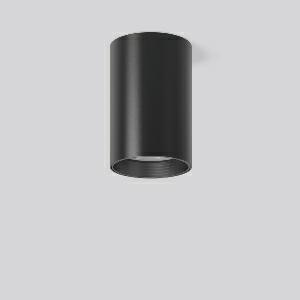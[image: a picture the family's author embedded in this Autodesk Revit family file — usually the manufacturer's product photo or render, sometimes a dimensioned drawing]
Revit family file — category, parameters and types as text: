
# Revit family: heledon_maxi_a_931228_003_1_76_a699
name_source: partatom
category: Lighting Fixtures
units: mm (PartAtom-declared; Revit-internal decimal feet)

## family parameters
Cut with Voids When Loaded = No
Host = Face
Light Source = No
Part Type = Normal
Room Calculation Point = No
Round Connector Dimension = Use Diameter
Shared = No

## types (1)
- HELEDON maxi A (1 x LED Modul 940, 3750 lm, 4000)
    Apparent Load = 35 VA
    Approval mark = CE
    CIE Flux Codes = 96 100 100 100 100
    Color Rendering = 92
    Color Temperature = 4000
    Default Elevation = 1800 mm
    Description = Series: HELEDON maxi
Cylindrical surface-mounted downlight. Housing: die-cast aluminium, powder-coated. Internal ceiling frame polycarbonate with bayonet mounting. Black plastic ring and recessed LED to prevent glare from the side. Optical assembly with lens made of plastic (polycarbonate) for the best homogeneous light distribution - can be changed without tools. Best colour rendering index Ra>90. Suitable for Ceiling mounting. Easy installation with a separate ceiling frame with bayonet mounting and plug connection. Driver integrated. Connected via plug-in connector. High quality converter without flickering and stroboscopic effect. The following accessories can be mounted without use of tools: interchangeable lenses, decorative glasses, honeycomb louvre, clear and frosted diffusers, white interchangeable plastic ring. 
Colour: deep black, matt (RAL 9005)
Diameter: 123 mm
Height: 183 mm
Lamp: LED
Socket: without socket
Colour temperature: 4000K
Colour rendering index (CRI): 92
System power: 35 W
Rated luminous flux: 3750 lm
Luminous efficiency: 107 lm/W
Control gear: Converter, dimmable, DALI
Protection class: I
Type of protection: IP 20
    Height = 183 mm
    Lamp = 1 x LED Modul 940
    Lamp Light Flux = 3750 lm
    Lamp count = 1
    Length = 123 mm
    Lifetime = 50000 h
    Luminous efficacy = 107 lm/W
    Manufacturer = RZB
    ModVariant = No
    Model = 931228.003.1.76
    Mounting Place = Ceiling
    Mounting Type = Surface mounted
    Number of Poles = 1
    OnlyDefault = Yes
    Power Factor = 1
    Product Name = HELEDON maxi A
    Product group = Surface mounted downlights
    ProductGroupID = 302
    Protection Class = Protection class I
    Protection Degree = IP 20
    RLX_Detail_Level = 1
    RLX_Emergency_Light_Flux = 0 lm
    RLX_Emergency_Type = 0
    RLX_Emergency_Type_DB = No
    RlxData = <blob elided: 97201 chars, md5=72847e4a>
    Socket = socket
    Standby Power = 0 W
    System Light Flux = 3750 lm
    System Power = 35 W
    Type Comments = Product without accessories
    Type Image = 931193.003.jpg
    URL = http://relux.com
    VarID = ---
    Voltage = 230 V
    Voltage Range = 220-240 V
    Weight = 0.00 kg
    Width = 0 mm  [stored 0 ft]

note: [stored X ft] marks values corroborated as IEEE doubles in the binary element streams (Revit-internal decimal feet)

## geometry (parser evidence)
native form markers: Blend x4, Sweep x11
no freeform markers — native parametric forms only
